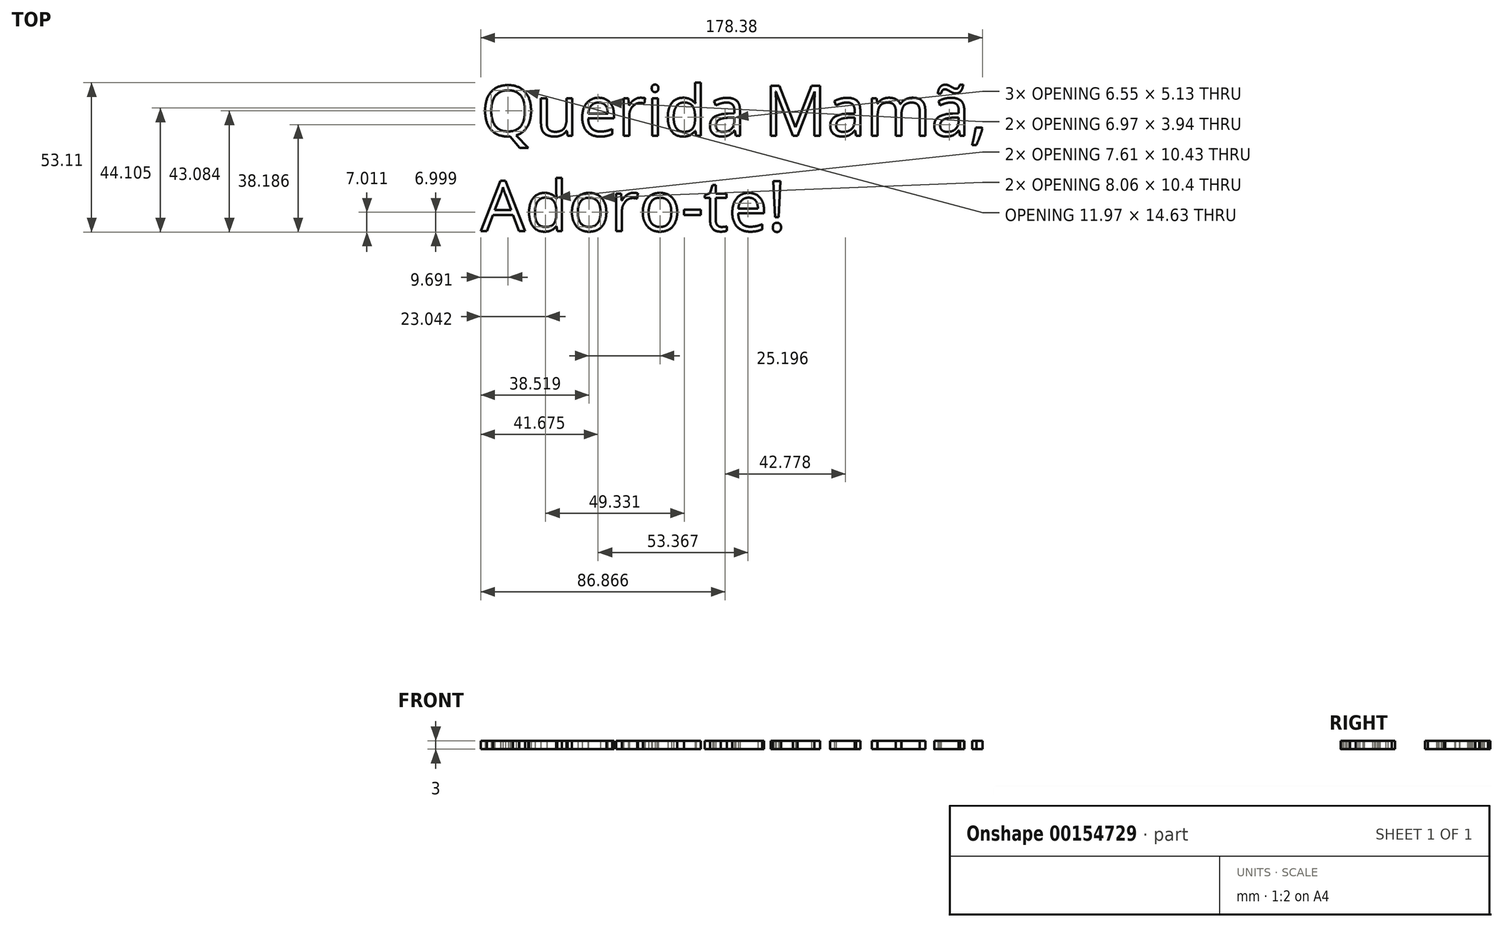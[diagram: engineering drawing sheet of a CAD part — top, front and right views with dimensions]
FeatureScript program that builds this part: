
annotation { "Feature Type Name" : "Feature", "Feature Type Description" : "" }
export const myFeature = defineFeature(function(context is Context, id is Id, definition is map)
    precondition{}
    {
        {
            var Q0;
            Q0=qCreatedBy(makeId("Top.planeOp"),FACE);
            var sketch = newSketch(context, id + "F0", { "sketchPlane" : qUnion([Q0])});
            skText(sketch, "E0", { "text": "Querida Mamã,\nAdoro-te!", "fontName": "OpenSans-Regular.ttf"});
            const initialGuessF0  = {"E0": [0, 0, 1, 0, 0.01792]};
            skSetInitialGuess(sketch, initialGuessF0);
            skSolve(sketch);
        }
        {
            var Q0;
            Q0 = qSketchRegion(id + "F0", true);
            extrude(context, id + "F1", {"entities" : qUnion([Q0]), "depth" : 3 * mm});
        }
    });
